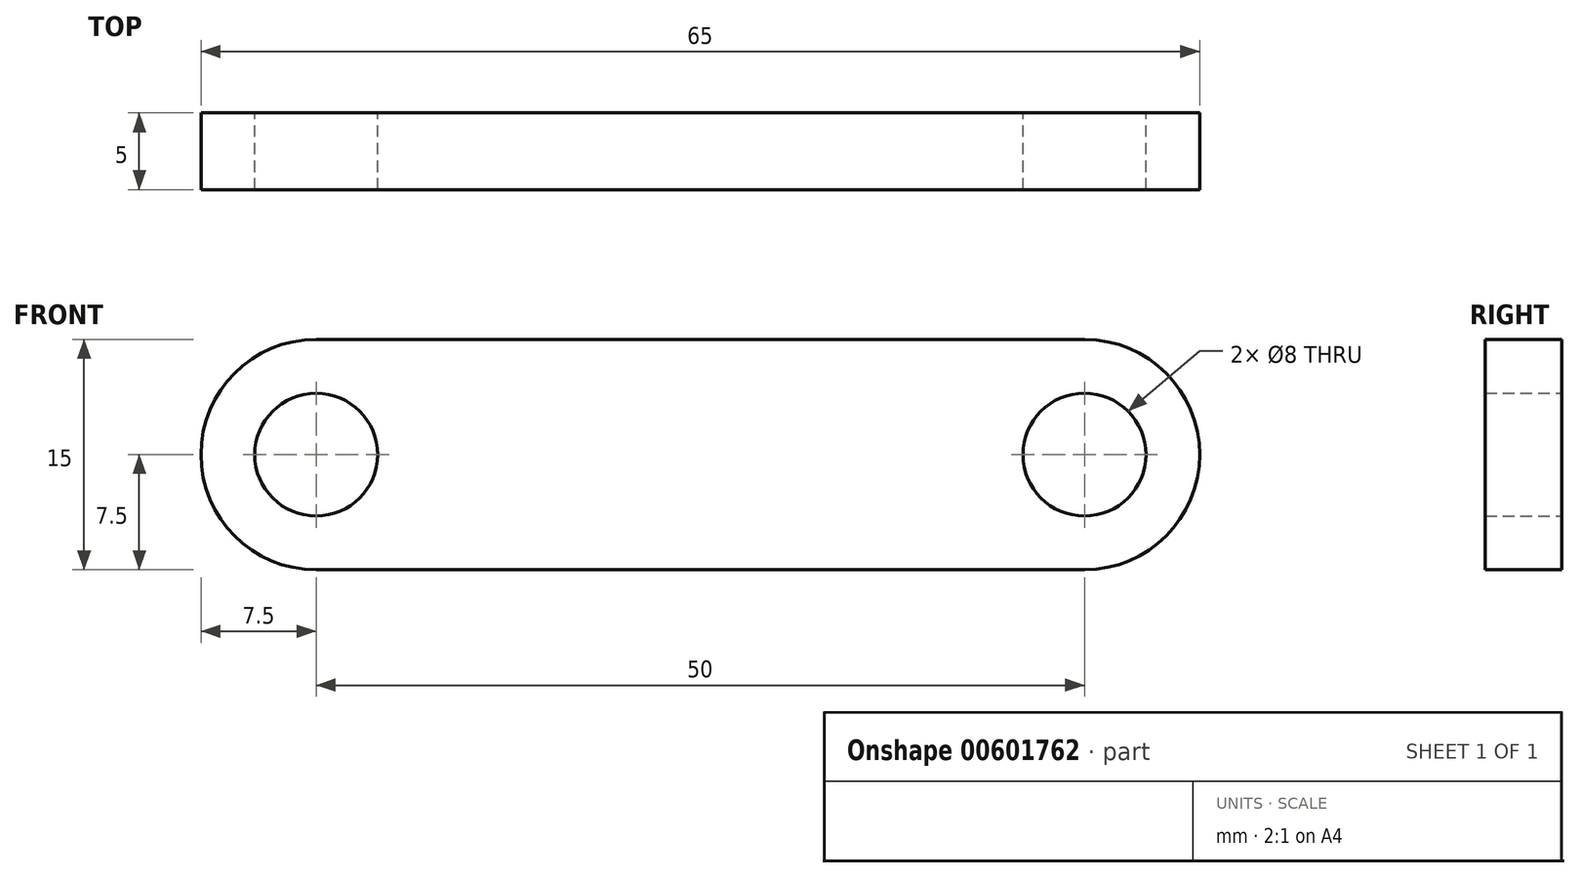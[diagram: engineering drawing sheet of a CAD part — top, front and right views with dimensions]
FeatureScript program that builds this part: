
annotation { "Feature Type Name" : "Feature", "Feature Type Description" : "" }
export const myFeature = defineFeature(function(context is Context, id is Id, definition is map)
    precondition{}
    {
        {
            var Q0;
            Q0=qCreatedBy(makeId("Front.planeOp"),FACE);
            var sketch = newSketch(context, id + "F0", { "sketchPlane" : qUnion([Q0])});
            skLineSegment(sketch, "E0", {"start": v(-25, 7.5) * mm, "end": v(25, 7.5) * mm});
            skLineSegment(sketch, "E1", {"start": v(-25, -7.5) * mm, "end": v(25, -7.5) * mm});
            skArc(sketch, "E2", {"start": v(25, -7.5) * mm, "mid": v(32.5, 0) * mm, "end": v(25, 7.5) * mm});
            skArc(sketch, "E3", {"start": v(-25, 7.5) * mm, "mid": v(-32.5, 0) * mm, "end": v(-25, -7.5) * mm});
            skCircle(sketch, "E4", {"center": v(-25, 0) * mm, "radius": 4 * mm});
            skCircle(sketch, "E5", {"center": v(25, 0) * mm, "radius": 4 * mm});
            skSolve(sketch);
        }
        {
            var Q0;
            Q0=makeQuery(id+"F0.imprint","IMPRINT",FACE,{"disambiguationData":[TD([[makeQuery(id+"F0.imprint","IMPRINT",EDGE,{"derivedFrom":sQuery(id+"F0.wireOp",EDGE,"E0")}),-1.0]])]});
            extrude(context, id + "F1", {"entities" : qUnion([Q0]), "depth" : 5 * mm, "offsetDistance" : 25 * mm});
        }
    });
